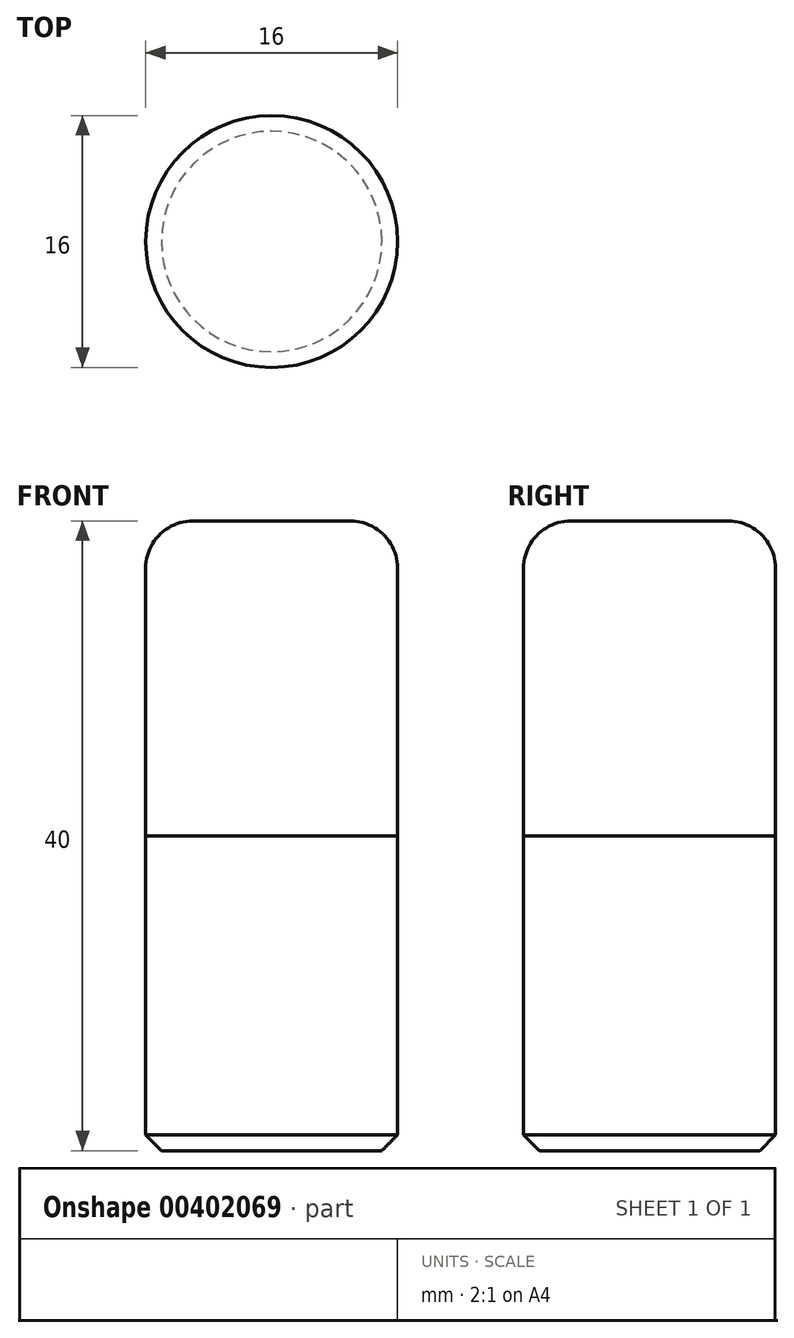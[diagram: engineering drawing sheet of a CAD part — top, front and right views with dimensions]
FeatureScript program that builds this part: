
annotation { "Feature Type Name" : "Feature", "Feature Type Description" : "" }
export const myFeature = defineFeature(function(context is Context, id is Id, definition is map)
    precondition{}
    {
        {
            var Q0;
            Q0=qCreatedBy(makeId("Top.planeOp"),FACE);
            var sketch = newSketch(context, id + "F0", { "sketchPlane" : qUnion([Q0])});
            skCircle(sketch, "E0", {"center": v(0, 0) * mm, "radius": 8 * mm});
            skSolve(sketch);
        }
        {
            var Q0;
            Q0 = qSketchRegion(id + "F0", true);
            extrude(context, id + "F1", {"entities" : qUnion([Q0]), "depth" : 20 * mm, "offsetDistance" : 25 * mm});
        }
        {
            var Q0;
            Q0=makeQuery(id+"F1.opExtrude","CAP_EDGE",EDGE,{"disambiguationData":[OSD([sQuery(id+"F0.wireOp",EDGE,"E0")])],"isStart":false});
            fillet(context, id + "F2", {"entities" : qUnion([Q0]), "radius" : 3 * mm, "tangentPropagation" : true, "allowEdgeOverflow" : false});
        }
        {
            var Q0;
            Q0=makeQuery(id+"F1.opExtrude","CAP_FACE",FACE,{"disambiguationData":[OSD([sQuery(id+"F0.wireOp",EDGE,"E0")])],"isStart":true});
            extrude(context, id + "F3", {"entities" : qUnion([Q0]), "depth" : 20 * mm, "offsetDistance" : 25 * mm});
        }
        {
            var Q0;
            Q0=makeQuery(id+"F3.opExtrude","CAP_FACE",FACE,{"disambiguationData":[OSD([sQuery(id+"F0.wireOp",EDGE,"E0")])],"isStart":false});
            chamfer(context, id + "F4", {"entities" : qUnion([Q0]), "width" : 1 * mm, "tangentPropagation" : true});
        }
    });
